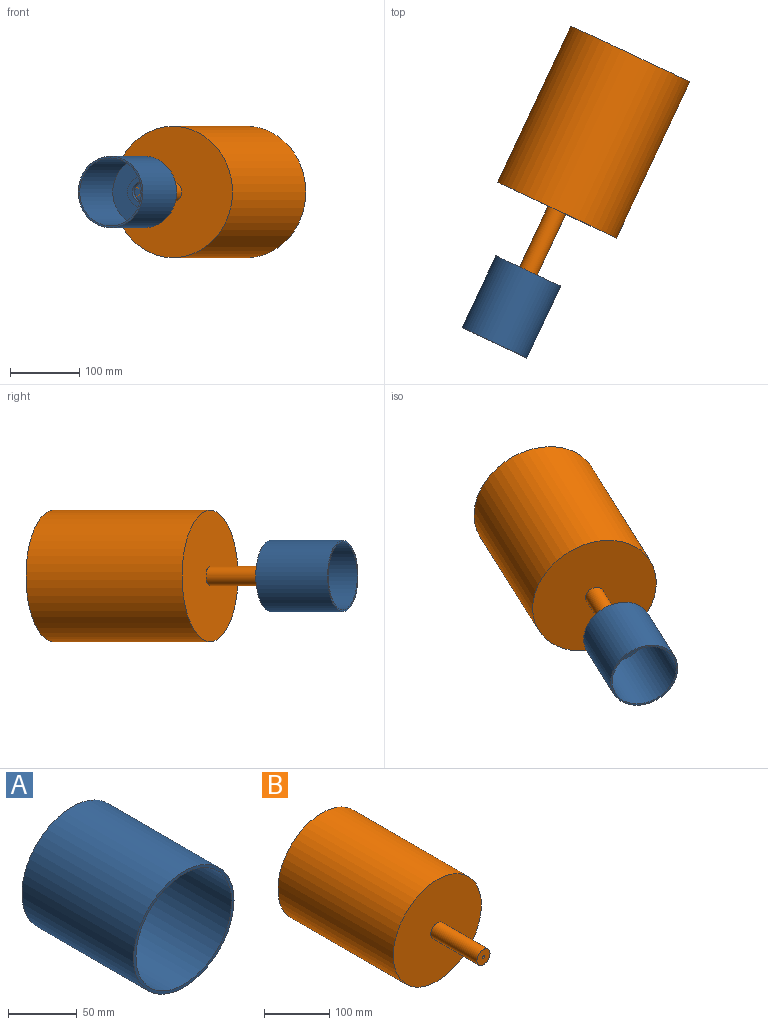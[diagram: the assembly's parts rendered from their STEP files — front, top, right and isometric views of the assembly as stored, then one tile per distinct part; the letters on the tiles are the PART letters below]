
ASSEMBLY  parts=2 mates=1
PART A: 10 faces, bbox 103.6x115x103.6 mm
  f0: cylinder r=51.78mm len=115mm, axis (0,1,0), area 37416.2mm2, adj f1,f9
  f1: plane 103.56x103.56mm, normal (0,1,0), area 8345.4mm2, adj f0,f8
  f2: cylinder r=49.28mm len=112.5mm, axis (0,1,0), area 34835.7mm2, adj f3,f9
  f3: plane 98.56x98.56mm, normal (0,-1,0), area 6092.7mm2, adj f2,f5
  f4: cylinder r=14.75mm len=29.49mm, axis (0,1,0), area 694.9mm2, adj f6,f7
  f5: cylinder r=22.12mm len=44.24mm, axis (0,1,0), area 1042.5mm2, adj f3,f6
  f6: plane 44.24x44.24mm, normal (0,-1,0), area 854.3mm2, adj f4,f5
  f7: plane 29.49x29.49mm, normal (0,-1,0), area 604.6mm2, adj f4,f8
  f8: cylinder r=5mm len=10mm, axis (0,1,0), area 78.5mm2, adj f1,f7
  f9: plane 103.56x103.56mm, normal (0,-1,0), area 793.8mm2, adj f0,f2
PART B: 6 faces, bbox 190.5x350x190.5 mm
  f0: cylinder r=95.23mm len=250mm, axis (0,1,0), area 149583.4mm2, adj f1,f4
  f1: plane 190.46x190.46mm, normal (0,-1,0), area 27864.4mm2, adj f0,f2
  f2: cylinder r=14.1mm len=100mm, axis (0,1,0), area 8859.4mm2, adj f1,f3
  f3: plane 28.2x28.2mm, normal (0,-1,0), area 605mm2, adj f2,f5
  f4: plane 190.46x190.46mm, normal (0,1,0), area 28469.4mm2, adj f0,f5
  f5: cylinder r=2.5mm len=350mm, axis (0,-1,0), area 5497.8mm2, adj f3,f4
PLACE A rot(axis=(-0.22,-0.98,0),180deg) t=(32.3,85.79,3.41)mm
PLACE B rot(axis=(0,0,-1),25.2deg) t=(95.01,219.3,3.41)mm
MATE revolute A.f0 <-> B.f0  axis (0.43,0.91,0) through (31.24,83.53,3.41)mm
